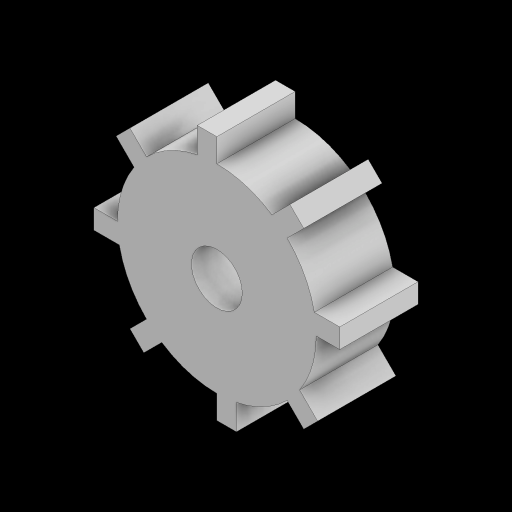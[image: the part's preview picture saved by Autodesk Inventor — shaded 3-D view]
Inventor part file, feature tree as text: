
AUTODESK INVENTOR PART (.ipt)
format: ipt  version: 2023 (Build 270158000, 158)  size: 162,304 bytes
history: native  units: mm
features: extrude x1, sketch x1
ambient origin geometry x8: Origin, YZ Plane, XZ Plane, XY Plane, X Axis, Y Axis, Z Axis, Center Point
bodies: Solid1 (feature_tree)
feature tree (2):
  extrude  "Extrusion1"  Depth=5.0mm TaperAngle=360.0deg
  sketch  "Sketch1"  dims[d2=1.5mm d4=80.0mm d6=360.0deg d8=5.0mm d9=0.0mm d10=3.25mm]
